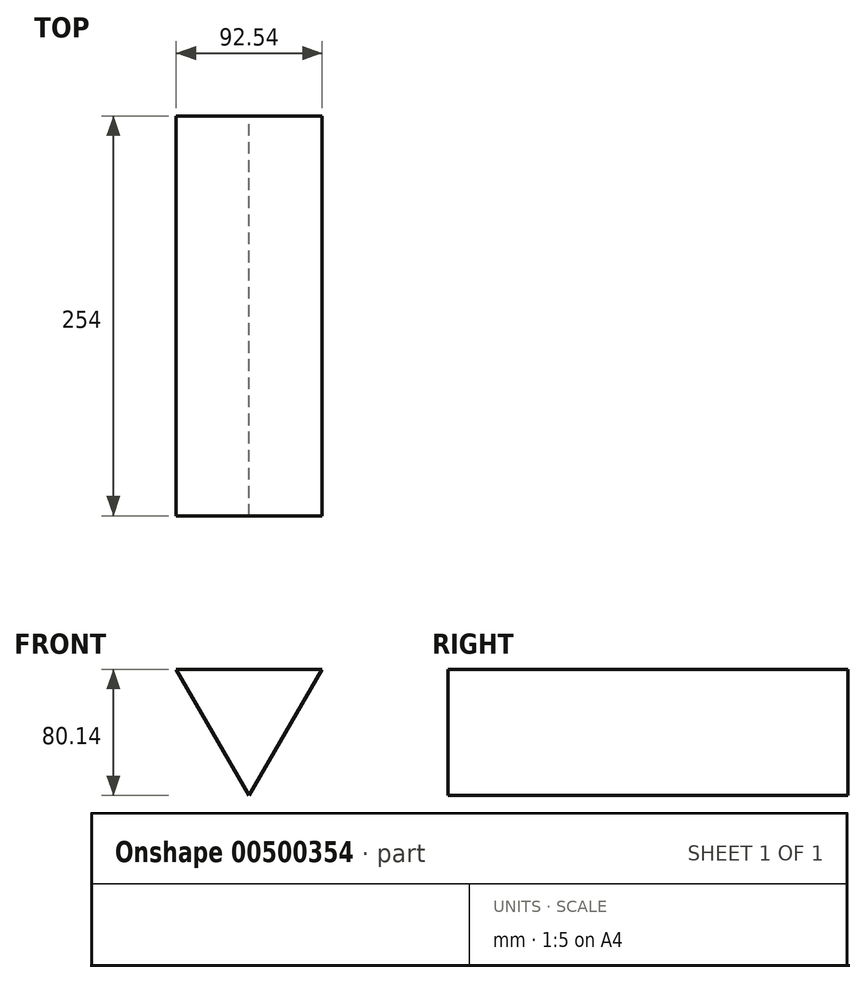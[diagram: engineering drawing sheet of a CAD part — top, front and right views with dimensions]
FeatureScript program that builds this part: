
annotation { "Feature Type Name" : "Feature", "Feature Type Description" : "" }
export const myFeature = defineFeature(function(context is Context, id is Id, definition is map)
    precondition{}
    {
        {
            var Q0;
            Q0=qCreatedBy(makeId("Front.planeOp"),FACE);
            var sketch = newSketch(context, id + "F0", { "sketchPlane" : qUnion([Q0])});
            skCircle(sketch, "E0.cCircle", {"center": v(0, 0) * mm, "radius": 53.43 * mm, "construction": true});
            skLineSegment(sketch, "E0.0", {"start": v(0, -53.43) * mm, "end": v(-46.27, 26.71) * mm});
            skLineSegment(sketch, "E0.1", {"start": v(-46.27, 26.71) * mm, "end": v(46.27, 26.71) * mm});
            skLineSegment(sketch, "E0.2", {"start": v(46.27, 26.71) * mm, "end": v(0, -53.43) * mm});
            skSolve(sketch);
        }
        {
            var Q0;
            Q0=makeQuery(id+"F0.imprint","IMPRINT",FACE,{"disambiguationData":[TD([[makeQuery(id+"F0.imprint","IMPRINT",EDGE,{"derivedFrom":sQuery(id+"F0.wireOp",EDGE,"E0.0")}),-1.0]])]});
            extrude(context, id + "F1", {"entities" : qUnion([Q0]), "endBound" : BoundingType.SYMMETRIC, "depth" : 254 * mm});
        }
    });
